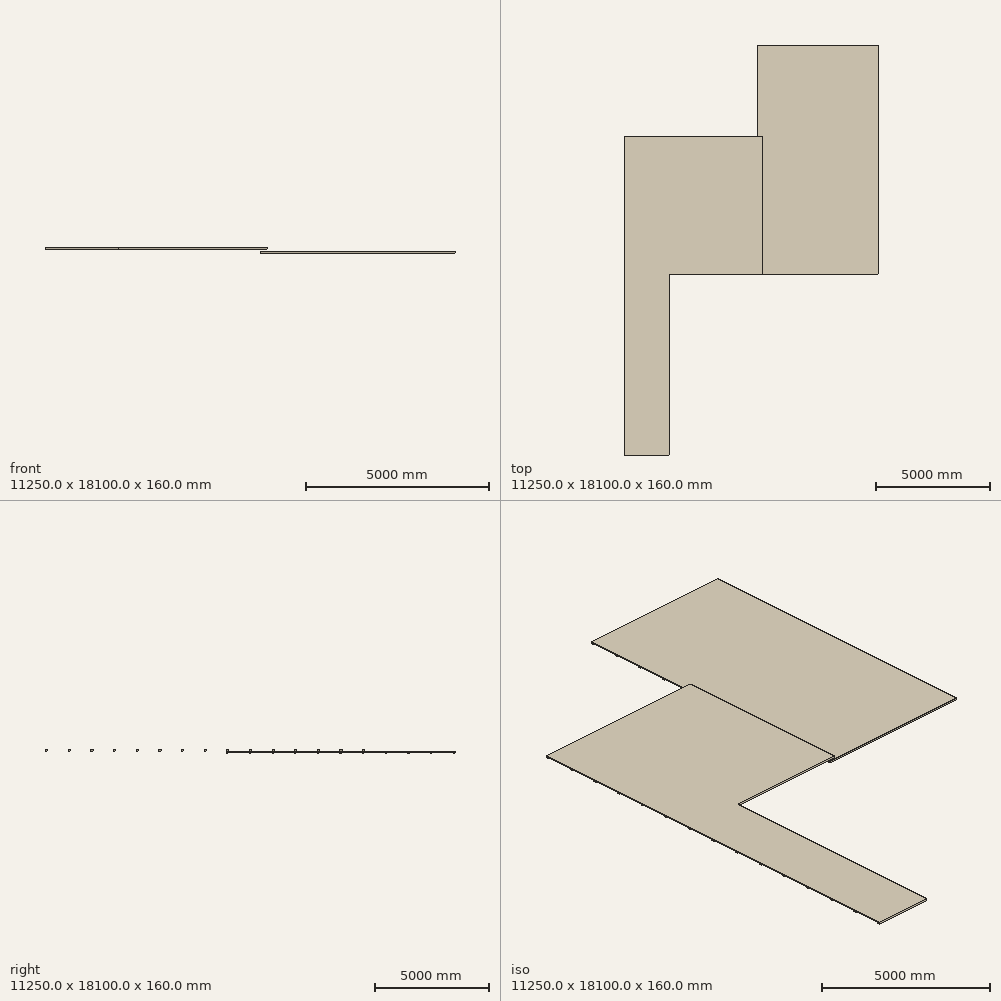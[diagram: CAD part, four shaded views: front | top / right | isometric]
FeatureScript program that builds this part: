
annotation { "Feature Type Name" : "Feature", "Feature Type Description" : "" }
export const myFeature = defineFeature(function(context is Context, id is Id, definition is map)
    precondition{}
    {
        {
            var Q0;
            Q0=qCreatedBy(makeId("Top.planeOp"),FACE);
            var sketch = newSketch(context, id + "F0", { "sketchPlane" : qUnion([Q0])});
            skLineSegment(sketch, "E0", {"start": v(0, 0) * mm, "end": v(0, 8000) * mm});
            skLineSegment(sketch, "E1", {"start": v(0, 8000) * mm, "end": v(9250, 8000) * mm});
            skLineSegment(sketch, "E2", {"start": v(0, 0) * mm, "end": v(-2000, 0) * mm});
            skLineSegment(sketch, "E3", {"start": v(-2000, 0) * mm, "end": v(-2000, 8000) * mm});
            skLineSegment(sketch, "E4", {"start": v(-2000, 8000) * mm, "end": v(-2000, 14100) * mm});
            skLineSegment(sketch, "E5", {"start": v(-2000, 14100) * mm, "end": v(3900, 14100) * mm});
            skLineSegment(sketch, "E6", {"start": v(3900, 14100) * mm, "end": v(3900, 18000) * mm});
            skLineSegment(sketch, "E7", {"start": v(3900, 18000) * mm, "end": v(9250, 18000) * mm});
            skLineSegment(sketch, "E8", {"start": v(9250, 18000) * mm, "end": v(9250, 8000) * mm});
            skLineSegment(sketch, "E9", {"start": v(3900, 14100) * mm, "end": v(3900, 8000) * mm});
            skLineSegment(sketch, "E10", {"start": v(3900, 14100) * mm, "end": v(4100, 14100) * mm});
            skLineSegment(sketch, "E11", {"start": v(4100, 14100) * mm, "end": v(4100, 8000) * mm});
            skSolve(sketch);
        }
        {
            var Q0;
            {var subQ2=sQuery(id+"F0.wireOp",EDGE,"E0");Q0=makeQuery(id+"F0.imprint","IMPRINT",FACE,{"disambiguationData":[TD([[makeQuery(id+"F0.imprint","IMPRINT",EDGE,{"derivedFrom":subQ2}),1.0]])]});}
            var Q1;
            {var subQ0=sQuery(id+"F0.wireOp",EDGE,"E9");Q1=makeQuery(id+"F0.imprint","IMPRINT",FACE,{"disambiguationData":[TD([[makeQuery(id+"F0.imprint","IMPRINT",EDGE,{"derivedFrom":subQ0}),1.0]])]});}
            extrude(context, id + "F1", {"entities" : qUnion([Q0, Q1]), "depth" : 10 * mm});
        }
        {
            var Q0;
            Q0=makeQuery(id+"F1.opExtrude","SWEPT_FACE",FACE,{"disambiguationData":[OSD([sQuery(id+"F0.wireOp",EDGE,"E3"),sQuery(id+"F0.wireOp",EDGE,"E4")])]});
            cPlane(context, id + "F2", {"entities" : qUnion([Q0]), "cplaneType" : CPlaneType.OFFSET, "offset" : 5900 * mm, "oppositeDirection" : true, "width" : 150 * mm, "height" : 150 * mm});
        }
        {
            var Q0;
            Q0=makeQuery(id+"F1.opExtrude","SWEPT_FACE",FACE,{"disambiguationData":[OSD([sQuery(id+"F0.wireOp",EDGE,"E3"),sQuery(id+"F0.wireOp",EDGE,"E4")])]});
            var sketch = newSketch(context, id + "F3", { "sketchPlane" : qUnion([Q0])});
            skLineSegment(sketch, "E12.bottom", {"start": v(-8000, 0) * mm, "end": v(-8100, 0) * mm});
            skLineSegment(sketch, "E12.top", {"start": v(-8000, -50) * mm, "end": v(-8100, -50) * mm});
            skLineSegment(sketch, "E12.left", {"start": v(-8000, 0) * mm, "end": v(-8000, -50) * mm});
            skLineSegment(sketch, "E12.right", {"start": v(-8100, 0) * mm, "end": v(-8100, -50) * mm});
            skLineSegment(sketch, "E13.0", {"start": v(-8000, 10) * mm, "end": v(-8000, 0) * mm, "construction": true});
            skLineSegment(sketch, "E14.1.0.0", {"start": v(-9000, -50) * mm, "end": v(-9100, -50) * mm});
            skLineSegment(sketch, "E14.1.0.1", {"start": v(-9000, 0) * mm, "end": v(-9100, 0) * mm});
            skLineSegment(sketch, "E14.1.0.2", {"start": v(-9100, 0) * mm, "end": v(-9100, -50) * mm});
            skLineSegment(sketch, "E14.1.0.3", {"start": v(-9000, 0) * mm, "end": v(-9000, -50) * mm});
            skLineSegment(sketch, "E14.2.0.0", {"start": v(-10000, -50) * mm, "end": v(-10100, -50) * mm});
            skLineSegment(sketch, "E14.2.0.1", {"start": v(-10000, 0) * mm, "end": v(-10100, 0) * mm});
            skLineSegment(sketch, "E14.2.0.2", {"start": v(-10100, 0) * mm, "end": v(-10100, -50) * mm});
            skLineSegment(sketch, "E14.2.0.3", {"start": v(-10000, 0) * mm, "end": v(-10000, -50) * mm});
            skLineSegment(sketch, "E14.direction1", {"start": v(-8100, -50) * mm, "end": v(-9100, -50) * mm, "construction": true});
            skLineSegment(sketch, "E15.0.3.0", {"start": v(-11000, -50) * mm, "end": v(-11100, -50) * mm});
            skLineSegment(sketch, "E15.3.3.0", {"start": v(-11000, 0) * mm, "end": v(-11100, 0) * mm});
            skLineSegment(sketch, "E15.6.3.0", {"start": v(-11100, 0) * mm, "end": v(-11100, -50) * mm});
            skLineSegment(sketch, "E15.9.3.0", {"start": v(-11000, 0) * mm, "end": v(-11000, -50) * mm});
            skLineSegment(sketch, "E15.0.4.0", {"start": v(-12000, -50) * mm, "end": v(-12100, -50) * mm});
            skLineSegment(sketch, "E15.3.4.0", {"start": v(-12000, 0) * mm, "end": v(-12100, 0) * mm});
            skLineSegment(sketch, "E15.6.4.0", {"start": v(-12100, 0) * mm, "end": v(-12100, -50) * mm});
            skLineSegment(sketch, "E15.9.4.0", {"start": v(-12000, 0) * mm, "end": v(-12000, -50) * mm});
            skLineSegment(sketch, "E15.0.5.0", {"start": v(-13000, -50) * mm, "end": v(-13100, -50) * mm});
            skLineSegment(sketch, "E15.3.5.0", {"start": v(-13000, 0) * mm, "end": v(-13100, 0) * mm});
            skLineSegment(sketch, "E15.6.5.0", {"start": v(-13100, 0) * mm, "end": v(-13100, -50) * mm});
            skLineSegment(sketch, "E15.9.5.0", {"start": v(-13000, 0) * mm, "end": v(-13000, -50) * mm});
            skLineSegment(sketch, "E15.0.6.0", {"start": v(-14000, -50) * mm, "end": v(-14100, -50) * mm});
            skLineSegment(sketch, "E15.3.6.0", {"start": v(-14000, 0) * mm, "end": v(-14100, 0) * mm});
            skLineSegment(sketch, "E15.6.6.0", {"start": v(-14100, 0) * mm, "end": v(-14100, -50) * mm});
            skLineSegment(sketch, "E15.9.6.0", {"start": v(-14000, 0) * mm, "end": v(-14000, -50) * mm});
            skSolve(sketch);
        }
        {
            var Q0;
            Q0 = qSketchRegion(id + "F3", true);
            extrude(context, id + "F4", {"entities" : qUnion([Q0]), "oppositeDirection" : true, "depth" : 6100 * mm});
        }
        {
            var Q0;
            Q0=makeQuery(id+"F1.opExtrude","SWEPT_FACE",FACE,{"disambiguationData":[OSD([sQuery(id+"F0.wireOp",EDGE,"E3"),sQuery(id+"F0.wireOp",EDGE,"E4")])]});
            var sketch = newSketch(context, id + "F5", { "sketchPlane" : qUnion([Q0])});
            skLineSegment(sketch, "E16.0.0", {"start": v(-8000, 0) * mm, "end": v(-8100, 0) * mm});
            skLineSegment(sketch, "E16.0.1", {"start": v(-8100, 0) * mm, "end": v(-8100, -50) * mm});
            skLineSegment(sketch, "E16.0.2", {"start": v(-8100, -50) * mm, "end": v(-8000, -50) * mm});
            skLineSegment(sketch, "E16.0.3", {"start": v(-8000, -50) * mm, "end": v(-8000, 0) * mm});
            skLineSegment(sketch, "E17.1.0.0", {"start": v(-7000, -50) * mm, "end": v(-7000, 0) * mm});
            skLineSegment(sketch, "E17.1.0.1", {"start": v(-7100, -50) * mm, "end": v(-7000, -50) * mm});
            skLineSegment(sketch, "E17.1.0.2", {"start": v(-7100, 0) * mm, "end": v(-7100, -50) * mm});
            skLineSegment(sketch, "E17.1.0.3", {"start": v(-7000, 0) * mm, "end": v(-7100, 0) * mm});
            skLineSegment(sketch, "E17.2.0.0", {"start": v(-6000, -50) * mm, "end": v(-6000, 0) * mm});
            skLineSegment(sketch, "E17.2.0.1", {"start": v(-6100, -50) * mm, "end": v(-6000, -50) * mm});
            skLineSegment(sketch, "E17.2.0.2", {"start": v(-6100, 0) * mm, "end": v(-6100, -50) * mm});
            skLineSegment(sketch, "E17.2.0.3", {"start": v(-6000, 0) * mm, "end": v(-6100, 0) * mm});
            skLineSegment(sketch, "E17.3.0.0", {"start": v(-5000, -50) * mm, "end": v(-5000, 0) * mm});
            skLineSegment(sketch, "E17.3.0.1", {"start": v(-5100, -50) * mm, "end": v(-5000, -50) * mm});
            skLineSegment(sketch, "E17.3.0.2", {"start": v(-5100, 0) * mm, "end": v(-5100, -50) * mm});
            skLineSegment(sketch, "E17.3.0.3", {"start": v(-5000, 0) * mm, "end": v(-5100, 0) * mm});
            skLineSegment(sketch, "E17.4.0.0", {"start": v(-4000, -50) * mm, "end": v(-4000, 0) * mm});
            skLineSegment(sketch, "E17.4.0.1", {"start": v(-4100, -50) * mm, "end": v(-4000, -50) * mm});
            skLineSegment(sketch, "E17.4.0.2", {"start": v(-4100, 0) * mm, "end": v(-4100, -50) * mm});
            skLineSegment(sketch, "E17.4.0.3", {"start": v(-4000, 0) * mm, "end": v(-4100, 0) * mm});
            skLineSegment(sketch, "E17.5.0.0", {"start": v(-3000, -50) * mm, "end": v(-3000, 0) * mm});
            skLineSegment(sketch, "E17.5.0.1", {"start": v(-3100, -50) * mm, "end": v(-3000, -50) * mm});
            skLineSegment(sketch, "E17.5.0.2", {"start": v(-3100, 0) * mm, "end": v(-3100, -50) * mm});
            skLineSegment(sketch, "E17.5.0.3", {"start": v(-3000, 0) * mm, "end": v(-3100, 0) * mm});
            skLineSegment(sketch, "E17.6.0.0", {"start": v(-2000, -50) * mm, "end": v(-2000, 0) * mm});
            skLineSegment(sketch, "E17.6.0.1", {"start": v(-2100, -50) * mm, "end": v(-2000, -50) * mm});
            skLineSegment(sketch, "E17.6.0.2", {"start": v(-2100, 0) * mm, "end": v(-2100, -50) * mm});
            skLineSegment(sketch, "E17.6.0.3", {"start": v(-2000, 0) * mm, "end": v(-2100, 0) * mm});
            skLineSegment(sketch, "E17.7.0.0", {"start": v(-1000, -50) * mm, "end": v(-1000, 0) * mm});
            skLineSegment(sketch, "E17.7.0.1", {"start": v(-1100, -50) * mm, "end": v(-1000, -50) * mm});
            skLineSegment(sketch, "E17.7.0.2", {"start": v(-1100, 0) * mm, "end": v(-1100, -50) * mm});
            skLineSegment(sketch, "E17.7.0.3", {"start": v(-1000, 0) * mm, "end": v(-1100, 0) * mm});
            skLineSegment(sketch, "E17.8.0.0", {"start": v(0, -50) * mm, "end": v(0, 0) * mm});
            skLineSegment(sketch, "E17.8.0.1", {"start": v(-100, -50) * mm, "end": v(0, -50) * mm});
            skLineSegment(sketch, "E17.8.0.2", {"start": v(-100, 0) * mm, "end": v(-100, -50) * mm});
            skLineSegment(sketch, "E17.8.0.3", {"start": v(0, 0) * mm, "end": v(-100, 0) * mm});
            skLineSegment(sketch, "E17.direction1", {"start": v(-8100, -50) * mm, "end": v(-7100, -50) * mm, "construction": true});
            skSolve(sketch);
        }
        {
            var Q0;
            Q0 = qSketchRegion(id + "F5", true);
            extrude(context, id + "F6", {"entities" : qUnion([Q0]), "operationType" : NewBodyOperationType.ADD, "oppositeDirection" : true, "depth" : 2000 * mm});
        }
        {
            var Q0;
            Q0=qCreatedBy(id+"F2.planeOp",FACE);
            var sketch = newSketch(context, id + "F7", { "sketchPlane" : qUnion([Q0])});
            skLineSegment(sketch, "E18.bottom", {"start": v(-8100, -100) * mm, "end": v(-8000, -100) * mm});
            skLineSegment(sketch, "E18.top", {"start": v(-8100, -150) * mm, "end": v(-8000, -150) * mm});
            skLineSegment(sketch, "E18.left", {"start": v(-8100, -100) * mm, "end": v(-8100, -150) * mm});
            skLineSegment(sketch, "E18.right", {"start": v(-8000, -100) * mm, "end": v(-8000, -150) * mm});
            skLineSegment(sketch, "E19.0.0", {"start": v(-8000, 0) * mm, "end": v(-8100, 0) * mm, "construction": true});
            skLineSegment(sketch, "E19.0.1", {"start": v(-8100, 0) * mm, "end": v(-8100, -50) * mm, "construction": true});
            skLineSegment(sketch, "E19.0.2", {"start": v(-8100, -50) * mm, "end": v(-8000, -50) * mm, "construction": true});
            skLineSegment(sketch, "E19.0.3", {"start": v(-8000, -50) * mm, "end": v(-8000, 0) * mm, "construction": true});
            skLineSegment(sketch, "E20", {"start": v(-8000, -100) * mm, "end": v(-8000, -50) * mm, "construction": true});
            skLineSegment(sketch, "E21", {"start": v(-8100, -100) * mm, "end": v(-8100, -50) * mm, "construction": true});
            skLineSegment(sketch, "E22.1.0.0", {"start": v(-9000, -100) * mm, "end": v(-9000, -150) * mm});
            skLineSegment(sketch, "E22.1.0.1", {"start": v(-9100, -100) * mm, "end": v(-9000, -100) * mm});
            skLineSegment(sketch, "E22.1.0.2", {"start": v(-9100, -150) * mm, "end": v(-9000, -150) * mm});
            skLineSegment(sketch, "E22.1.0.3", {"start": v(-9100, -100) * mm, "end": v(-9100, -150) * mm});
            skLineSegment(sketch, "E22.2.0.0", {"start": v(-10000, -100) * mm, "end": v(-10000, -150) * mm});
            skLineSegment(sketch, "E22.2.0.1", {"start": v(-10100, -100) * mm, "end": v(-10000, -100) * mm});
            skLineSegment(sketch, "E22.2.0.2", {"start": v(-10100, -150) * mm, "end": v(-10000, -150) * mm});
            skLineSegment(sketch, "E22.2.0.3", {"start": v(-10100, -100) * mm, "end": v(-10100, -150) * mm});
            skLineSegment(sketch, "E22.3.0.0", {"start": v(-11000, -100) * mm, "end": v(-11000, -150) * mm});
            skLineSegment(sketch, "E22.3.0.1", {"start": v(-11100, -100) * mm, "end": v(-11000, -100) * mm});
            skLineSegment(sketch, "E22.3.0.2", {"start": v(-11100, -150) * mm, "end": v(-11000, -150) * mm});
            skLineSegment(sketch, "E22.3.0.3", {"start": v(-11100, -100) * mm, "end": v(-11100, -150) * mm});
            skLineSegment(sketch, "E22.4.0.0", {"start": v(-12000, -100) * mm, "end": v(-12000, -150) * mm});
            skLineSegment(sketch, "E22.4.0.1", {"start": v(-12100, -100) * mm, "end": v(-12000, -100) * mm});
            skLineSegment(sketch, "E22.4.0.2", {"start": v(-12100, -150) * mm, "end": v(-12000, -150) * mm});
            skLineSegment(sketch, "E22.4.0.3", {"start": v(-12100, -100) * mm, "end": v(-12100, -150) * mm});
            skLineSegment(sketch, "E22.5.0.0", {"start": v(-13000, -100) * mm, "end": v(-13000, -150) * mm});
            skLineSegment(sketch, "E22.5.0.1", {"start": v(-13100, -100) * mm, "end": v(-13000, -100) * mm});
            skLineSegment(sketch, "E22.5.0.2", {"start": v(-13100, -150) * mm, "end": v(-13000, -150) * mm});
            skLineSegment(sketch, "E22.5.0.3", {"start": v(-13100, -100) * mm, "end": v(-13100, -150) * mm});
            skLineSegment(sketch, "E22.6.0.0", {"start": v(-14000, -100) * mm, "end": v(-14000, -150) * mm});
            skLineSegment(sketch, "E22.6.0.1", {"start": v(-14100, -100) * mm, "end": v(-14000, -100) * mm});
            skLineSegment(sketch, "E22.6.0.2", {"start": v(-14100, -150) * mm, "end": v(-14000, -150) * mm});
            skLineSegment(sketch, "E22.6.0.3", {"start": v(-14100, -100) * mm, "end": v(-14100, -150) * mm});
            skLineSegment(sketch, "E22.7.0.0", {"start": v(-15000, -100) * mm, "end": v(-15000, -150) * mm});
            skLineSegment(sketch, "E22.7.0.1", {"start": v(-15100, -100) * mm, "end": v(-15000, -100) * mm});
            skLineSegment(sketch, "E22.7.0.2", {"start": v(-15100, -150) * mm, "end": v(-15000, -150) * mm});
            skLineSegment(sketch, "E22.7.0.3", {"start": v(-15100, -100) * mm, "end": v(-15100, -150) * mm});
            skLineSegment(sketch, "E22.8.0.0", {"start": v(-16000, -100) * mm, "end": v(-16000, -150) * mm});
            skLineSegment(sketch, "E22.8.0.1", {"start": v(-16100, -100) * mm, "end": v(-16000, -100) * mm});
            skLineSegment(sketch, "E22.8.0.2", {"start": v(-16100, -150) * mm, "end": v(-16000, -150) * mm});
            skLineSegment(sketch, "E22.8.0.3", {"start": v(-16100, -100) * mm, "end": v(-16100, -150) * mm});
            skLineSegment(sketch, "E22.9.0.0", {"start": v(-17000, -100) * mm, "end": v(-17000, -150) * mm});
            skLineSegment(sketch, "E22.9.0.1", {"start": v(-17100, -100) * mm, "end": v(-17000, -100) * mm});
            skLineSegment(sketch, "E22.9.0.2", {"start": v(-17100, -150) * mm, "end": v(-17000, -150) * mm});
            skLineSegment(sketch, "E22.9.0.3", {"start": v(-17100, -100) * mm, "end": v(-17100, -150) * mm});
            skLineSegment(sketch, "E22.10.0.0", {"start": v(-18000, -100) * mm, "end": v(-18000, -150) * mm});
            skLineSegment(sketch, "E22.10.0.1", {"start": v(-18100, -100) * mm, "end": v(-18000, -100) * mm});
            skLineSegment(sketch, "E22.10.0.2", {"start": v(-18100, -150) * mm, "end": v(-18000, -150) * mm});
            skLineSegment(sketch, "E22.10.0.3", {"start": v(-18100, -100) * mm, "end": v(-18100, -150) * mm});
            skLineSegment(sketch, "E22.direction1", {"start": v(-8100, -150) * mm, "end": v(-9100, -150) * mm, "construction": true});
            skSolve(sketch);
        }
        {
            var Q0;
            Q0 = qSketchRegion(id + "F7", true);
            extrude(context, id + "F8", {"entities" : qUnion([Q0]), "oppositeDirection" : true, "depth" : 5350 * mm});
        }
        {
            var Q0;
            Q0=qCreatedBy(id+"F2.planeOp",FACE);
            var sketch = newSketch(context, id + "F9", { "sketchPlane" : qUnion([Q0])});
            skLineSegment(sketch, "E23.0.0", {"start": v(-8100, -100) * mm, "end": v(-8100, -150) * mm, "construction": true});
            skLineSegment(sketch, "E23.0.1", {"start": v(-8100, -150) * mm, "end": v(-8000, -150) * mm, "construction": true});
            skLineSegment(sketch, "E23.0.2", {"start": v(-8000, -150) * mm, "end": v(-8000, -100) * mm, "construction": true});
            skLineSegment(sketch, "E23.0.3", {"start": v(-8000, -100) * mm, "end": v(-8100, -100) * mm, "construction": true});
            skLineSegment(sketch, "E24.bottom", {"start": v(-8000, -100) * mm, "end": v(-18100, -100) * mm});
            skLineSegment(sketch, "E24.top", {"start": v(-8000, -90) * mm, "end": v(-18100, -90) * mm});
            skLineSegment(sketch, "E24.left", {"start": v(-8000, -100) * mm, "end": v(-8000, -90) * mm});
            skLineSegment(sketch, "E24.right", {"start": v(-18100, -100) * mm, "end": v(-18100, -90) * mm});
            skLineSegment(sketch, "E25.0", {"start": v(-18100, -100) * mm, "end": v(-18100, -150) * mm, "construction": true});
            skLineSegment(sketch, "E25.1.0", {"start": v(-18000, -100) * mm, "end": v(-18100, -100) * mm, "construction": true});
            skLineSegment(sketch, "E25.1.1", {"start": v(-18100, -100) * mm, "end": v(-18100, -150) * mm, "construction": true});
            skLineSegment(sketch, "E25.1.2", {"start": v(-18100, -150) * mm, "end": v(-18000, -150) * mm, "construction": true});
            skLineSegment(sketch, "E25.1.3", {"start": v(-18000, -150) * mm, "end": v(-18000, -100) * mm, "construction": true});
            skSolve(sketch);
        }
        {
            var Q0;
            Q0 = qSketchRegion(id + "F9", true);
            var Q1;
            Q1=makeQuery(id+"F8.opExtrude","CAP_FACE",FACE,{"disambiguationData":[OSD([sQuery(id+"F7.wireOp",EDGE,"E22.10.0.0"),sQuery(id+"F7.wireOp",EDGE,"E22.10.0.1"),sQuery(id+"F7.wireOp",EDGE,"E22.10.0.2"),sQuery(id+"F7.wireOp",EDGE,"E22.10.0.3")])],"isStart":false});
            extrude(context, id + "F10", {"entities" : qUnion([Q0]), "endBound" : BoundingType.UP_TO_SURFACE, "oppositeDirection" : true, "endBoundEntityFace" : qUnion([Q1]), "depth" : 25 * mm});
        }
    });
